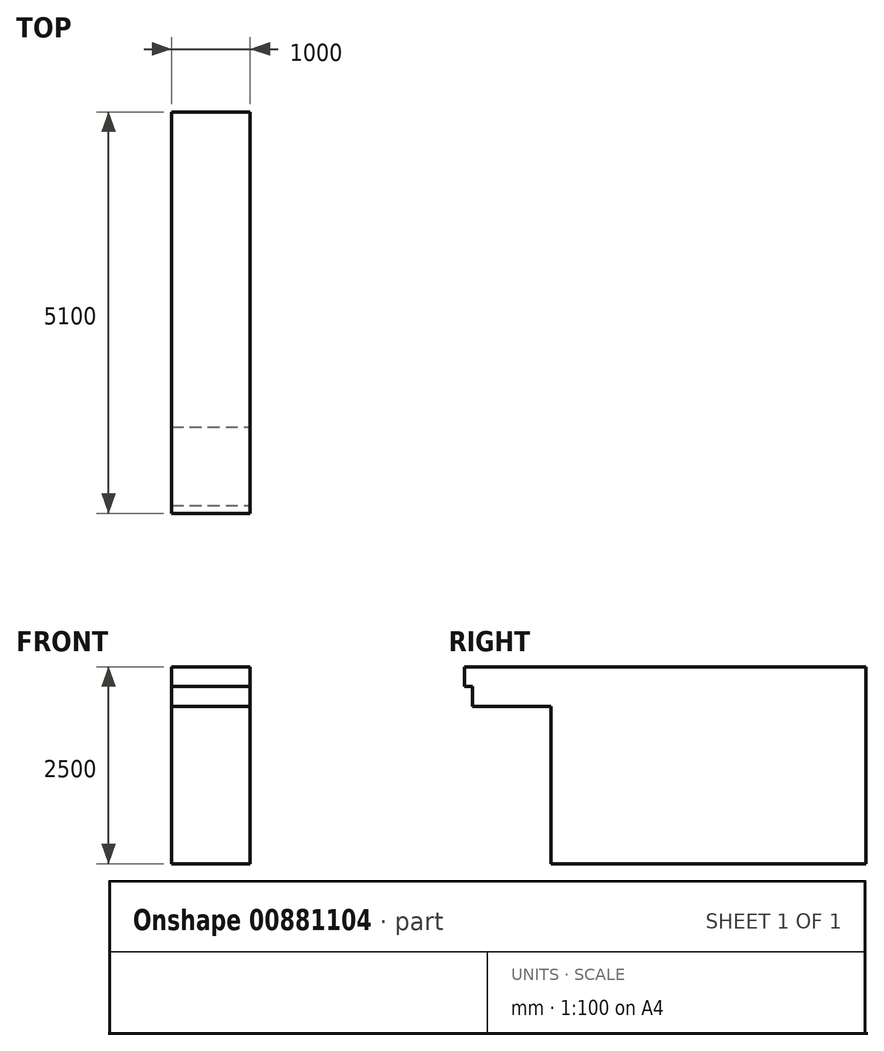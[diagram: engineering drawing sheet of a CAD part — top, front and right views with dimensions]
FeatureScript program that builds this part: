
annotation { "Feature Type Name" : "Feature", "Feature Type Description" : "" }
export const myFeature = defineFeature(function(context is Context, id is Id, definition is map)
    precondition{}
    {
        {
            var Q0;
            Q0=qCreatedBy(makeId("Top.planeOp"),FACE);
            var sketch = newSketch(context, id + "F0", { "sketchPlane" : qUnion([Q0])});
            skLineSegment(sketch, "E0", {"start": v(0, 0) * mm, "end": v(-500, 0) * mm});
            skLineSegment(sketch, "E1", {"start": v(-500, 0) * mm, "end": v(-500, 5000) * mm});
            skLineSegment(sketch, "E2", {"start": v(-500, 5000) * mm, "end": v(0, 5000) * mm});
            skLineSegment(sketch, "E3", {"start": v(0, 5000) * mm, "end": v(0, 0) * mm, "construction": true});
            skLineSegment(sketch, "E4.MirrorCS", {"start": v(0, 0) * mm, "end": v(500, 0) * mm});
            skLineSegment(sketch, "E5.MirrorCS", {"start": v(500, 5000) * mm, "end": v(0, 5000) * mm});
            skLineSegment(sketch, "E6.MirrorCS", {"start": v(500, 0) * mm, "end": v(500, 5000) * mm});
            skSolve(sketch);
        }
        {
            var Q0;
            Q0=makeQuery(id+"F0.imprint","IMPRINT",FACE,{"disambiguationData":[TD([[makeQuery(id+"F0.imprint","IMPRINT",EDGE,{"derivedFrom":sQuery(id+"F0.wireOp",EDGE,"E0")}),-1.0]])]});
            extrude(context, id + "F1", {"entities" : qUnion([Q0]), "depth" : 500 * mm, "offsetDistance" : 25 * mm});
        }
        {
            var Q0;
            Q0=makeQuery(id+"F1.opExtrude","CAP_FACE",FACE,{"disambiguationData":[OSD([sQuery(id+"F0.wireOp",EDGE,"E0"),sQuery(id+"F0.wireOp",EDGE,"E1"),sQuery(id+"F0.wireOp",EDGE,"E2"),sQuery(id+"F0.wireOp",EDGE,"E4.MirrorCS"),sQuery(id+"F0.wireOp",EDGE,"E5.MirrorCS"),sQuery(id+"F0.wireOp",EDGE,"E6.MirrorCS")])],"isStart":true});
            var sketch = newSketch(context, id + "F2", { "sketchPlane" : qUnion([Q0])});
            skLineSegment(sketch, "E7", {"start": v(-500, -1000) * mm, "end": v(500, -1000) * mm});
            skSolve(sketch);
        }
        {
            var Q0;
            {var subQ0=sQuery(id+"F2.wireOp",EDGE,"E7");Q0=makeQuery(id+"F2.imprint","IMPRINT",FACE,{"disambiguationData":[TD([[makeQuery(id+"F2.imprint","IMPRINT",EDGE,{"derivedFrom":subQ0}),-1.0]])]});}
            extrude(context, id + "F3", {"entities" : qUnion([Q0]), "operationType" : NewBodyOperationType.ADD, "depth" : 2000 * mm, "offsetDistance" : 25 * mm});
        }
        {
            var Q0;
            Q0=makeQuery(id+"F1.opExtrude","SWEPT_FACE",FACE,{"disambiguationData":[OSD([sQuery(id+"F0.wireOp",EDGE,"E0"),sQuery(id+"F0.wireOp",EDGE,"E4.MirrorCS")])]});
            var sketch = newSketch(context, id + "F4", { "sketchPlane" : qUnion([Q0])});
            skLineSegment(sketch, "E8", {"start": v(-500, 250) * mm, "end": v(500, 250) * mm});
            skSolve(sketch);
        }
        {
            var Q0;
            {var subQ0=sQuery(id+"F4.wireOp",EDGE,"E8");Q0=makeQuery(id+"F4.imprint","IMPRINT",FACE,{"disambiguationData":[TD([[makeQuery(id+"F4.imprint","IMPRINT",EDGE,{"derivedFrom":subQ0}),1.0]])]});}
            extrude(context, id + "F5", {"entities" : qUnion([Q0]), "operationType" : NewBodyOperationType.ADD, "depth" : 100 * mm, "offsetDistance" : 25 * mm});
        }
    });
